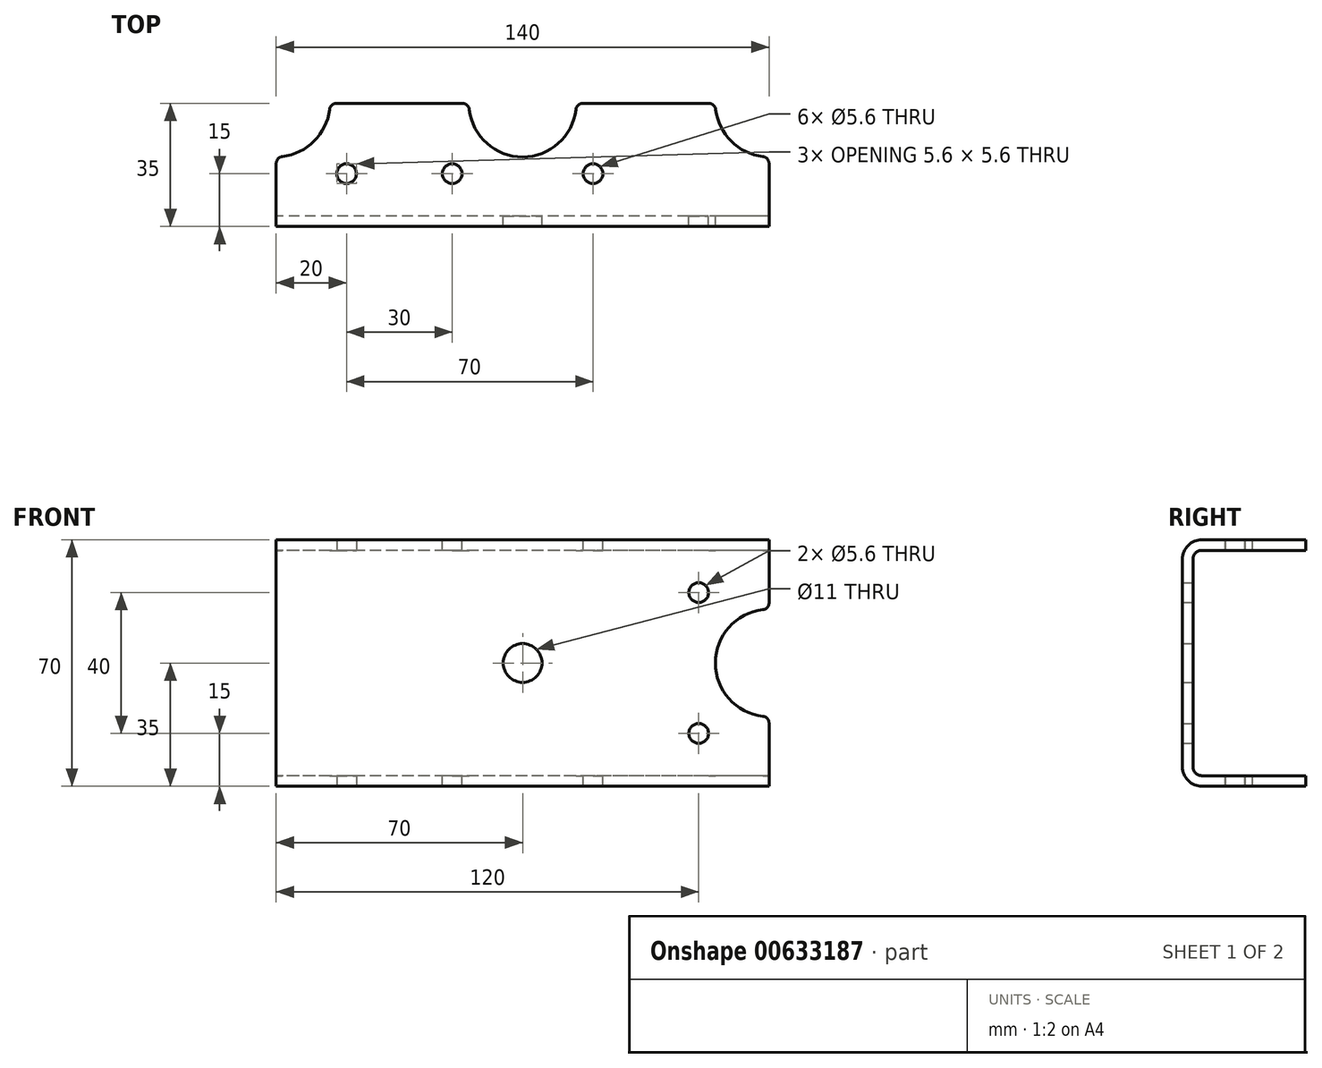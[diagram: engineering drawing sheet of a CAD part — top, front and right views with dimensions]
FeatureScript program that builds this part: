
annotation { "Feature Type Name" : "Feature", "Feature Type Description" : "" }
export const myFeature = defineFeature(function(context is Context, id is Id, definition is map)
    precondition{}
    {
        {
            var Q0;
            Q0=qCreatedBy(makeId("Front.planeOp"),FACE);
            var sketch = newSketch(context, id + "F0", { "sketchPlane" : qUnion([Q0])});
            skLineSegment(sketch, "E0.bottom", {"start": v(0, -32) * mm, "end": v(-32, -32) * mm});
            skLineSegment(sketch, "E0.top", {"start": v(0, 32) * mm, "end": v(-32, 32) * mm});
            skLineSegment(sketch, "E0.left", {"start": v(0, -32) * mm, "end": v(0, 32) * mm, "construction": true});
            skLineSegment(sketch, "E0.right", {"start": v(-32, -32) * mm, "end": v(-32, 32) * mm});
            skLineSegment(sketch, "E1.0", {"start": v(0, -35) * mm, "end": v(-35, -35) * mm});
            skLineSegment(sketch, "E1.1", {"start": v(-35, -35) * mm, "end": v(-35, 35) * mm});
            skLineSegment(sketch, "E1.2", {"start": v(0, 35) * mm, "end": v(-35, 35) * mm});
            skLineSegment(sketch, "E2", {"start": v(0, 35) * mm, "end": v(0, 32) * mm});
            skLineSegment(sketch, "E3", {"start": v(0, -32) * mm, "end": v(0, -35) * mm});
            skSolve(sketch);
        }
        {
            var Q0;
            Q0=makeQuery(id+"F0.imprint","IMPRINT",FACE,{"disambiguationData":[TD([[makeQuery(id+"F0.imprint","IMPRINT",EDGE,{"derivedFrom":sQuery(id+"F0.wireOp",EDGE,"E0.bottom")}),1.0]])]});
            extrude(context, id + "F1", {"entities" : qUnion([Q0]), "endBound" : BoundingType.SYMMETRIC, "depth" : 140 * mm});
        }
        {
            var Q0;
            Q0=makeQuery(id+"F1.opExtrude","SWEPT_EDGE",EDGE,{"disambiguationData":[OSD([sQuery(id+"F0.wireOp",EDGE,"E1.0"),sQuery(id+"F0.wireOp",EDGE,"E1.1")])]});
            var Q1;
            Q1=makeQuery(id+"F1.opExtrude","SWEPT_EDGE",EDGE,{"disambiguationData":[OSD([sQuery(id+"F0.wireOp",EDGE,"E1.1"),sQuery(id+"F0.wireOp",EDGE,"E1.2")])]});
            fillet(context, id + "F2", {"entities" : qUnion([Q0, Q1]), "radius" : 5.5 * mm, "tangentPropagation" : true, "allowEdgeOverflow" : false});
        }
        {
            var Q0;
            Q0=makeQuery(id+"F1.opExtrude","SWEPT_EDGE",EDGE,{"disambiguationData":[OSD([sQuery(id+"F0.wireOp",EDGE,"E0.top"),sQuery(id+"F0.wireOp",EDGE,"E0.right")])]});
            var Q1;
            Q1=makeQuery(id+"F1.opExtrude","SWEPT_EDGE",EDGE,{"disambiguationData":[OSD([sQuery(id+"F0.wireOp",EDGE,"E0.bottom"),sQuery(id+"F0.wireOp",EDGE,"E0.right")])]});
            fillet(context, id + "F3", {"entities" : qUnion([Q0, Q1]), "radius" : 2.5 * mm, "tangentPropagation" : true, "allowEdgeOverflow" : false});
        }
        {
            var Q0;
            Q0=qCreatedBy(makeId("Top.planeOp"),FACE);
            var sketch = newSketch(context, id + "F4", { "sketchPlane" : qUnion([Q0])});
            skCircle(sketch, "E4", {"center": v(0, -70) * mm, "radius": 15.25 * mm});
            skCircle(sketch, "E5", {"center": v(0, 70) * mm, "radius": 15.25 * mm});
            skSolve(sketch);
        }
        {
            var Q0;
            Q0=qSketchRegion(id+"F4",true);
            extrude(context, id + "F5", {"entities" : qUnion([Q0]), "operationType" : NewBodyOperationType.REMOVE, "endBound" : BoundingType.SYMMETRIC, "oppositeDirection" : true, "depth" : 70 * mm});
        }
        {
            var Q0;
            Q0=qCreatedBy(makeId("Top.planeOp"),FACE);
            var sketch = newSketch(context, id + "F6", { "sketchPlane" : qUnion([Q0])});
            skCircle(sketch, "E6", {"center": v(0, 0) * mm, "radius": 15.25 * mm});
            skSolve(sketch);
        }
        {
            var Q0;
            Q0=qSketchRegion(id+"F6",true);
            extrude(context, id + "F7", {"entities" : qUnion([Q0]), "operationType" : NewBodyOperationType.REMOVE, "endBound" : BoundingType.SYMMETRIC, "depth" : 70 * mm});
        }
        {
            var Q0;
            Q0=qCreatedBy(makeId("Top.planeOp"),FACE);
            var sketch = newSketch(context, id + "F8", { "sketchPlane" : qUnion([Q0])});
            skCircle(sketch, "E7", {"center": v(-20, 50) * mm, "radius": 2.8 * mm});
            skSolve(sketch);
        }
        {
            var Q0;
            Q0=qSketchRegion(id+"F8",true);
            extrude(context, id + "F9", {"entities" : qUnion([Q0]), "operationType" : NewBodyOperationType.REMOVE, "endBound" : BoundingType.SYMMETRIC, "depth" : 70 * mm});
        }
        {
            var Q0;
            Q0=qCreatedBy(makeId("Top.planeOp"),FACE);
            var sketch = newSketch(context, id + "F10", { "sketchPlane" : qUnion([Q0])});
            skCircle(sketch, "E8", {"center": v(-20, -20) * mm, "radius": 2.8 * mm});
            skCircle(sketch, "E9", {"center": v(-20, 20) * mm, "radius": 2.8 * mm});
            skSolve(sketch);
        }
        {
            var Q0;
            Q0=qSketchRegion(id+"F10",true);
            extrude(context, id + "F11", {"entities" : qUnion([Q0]), "operationType" : NewBodyOperationType.REMOVE, "endBound" : BoundingType.SYMMETRIC, "oppositeDirection" : true, "depth" : 70 * mm});
        }
        {
            var Q0;
            Q0=qCreatedBy(makeId("Right.planeOp"),FACE);
            var sketch = newSketch(context, id + "F12", { "sketchPlane" : qUnion([Q0])});
            skCircle(sketch, "E10", {"center": v(-70, 0) * mm, "radius": 15.25 * mm});
            skCircle(sketch, "E11", {"center": v(-50, 20) * mm, "radius": 2.8 * mm});
            skCircle(sketch, "E12", {"center": v(-50, -20) * mm, "radius": 2.8 * mm});
            skSolve(sketch);
        }
        {
            var Q0;
            Q0=qSketchRegion(id+"F12",true);
            extrude(context, id + "F13", {"entities" : qUnion([Q0]), "operationType" : NewBodyOperationType.REMOVE, "endBound" : BoundingType.THROUGH_ALL, "oppositeDirection" : true, "depth" : 25 * mm});
        }
        {
            var Q0;
            Q0=makeQuery(id+"F7.boolean.opBoolean","INTERSECT",EDGE,{"disambiguationData":[OD(0.0)],"derivedFrom":[makeQuery(id+"F1.opExtrude","SWEPT_FACE",FACE,{"disambiguationData":[OSD([sQuery(id+"F0.wireOp",EDGE,"E2")])]}),makeQuery(id+"F7.opExtrude","SWEPT_FACE",FACE,{"disambiguationData":[OSD([sQuery(id+"F6.wireOp",EDGE,"E6")])]})]});
            var Q1;
            Q1=makeQuery(id+"F7.boolean.opBoolean","INTERSECT",EDGE,{"disambiguationData":[OD(1.0)],"derivedFrom":[makeQuery(id+"F1.opExtrude","SWEPT_FACE",FACE,{"disambiguationData":[OSD([sQuery(id+"F0.wireOp",EDGE,"E2")])]}),makeQuery(id+"F7.opExtrude","SWEPT_FACE",FACE,{"disambiguationData":[OSD([sQuery(id+"F6.wireOp",EDGE,"E6")])]})]});
            var Q2;
            Q2=makeQuery(id+"F7.boolean.opBoolean","INTERSECT",EDGE,{"disambiguationData":[OD(1.0)],"derivedFrom":[makeQuery(id+"F1.opExtrude","SWEPT_FACE",FACE,{"disambiguationData":[OSD([sQuery(id+"F0.wireOp",EDGE,"E3")])]}),makeQuery(id+"F7.opExtrude","SWEPT_FACE",FACE,{"disambiguationData":[OSD([sQuery(id+"F6.wireOp",EDGE,"E6")])]})]});
            var Q3;
            Q3=makeQuery(id+"F7.boolean.opBoolean","INTERSECT",EDGE,{"disambiguationData":[OD(0.0)],"derivedFrom":[makeQuery(id+"F1.opExtrude","SWEPT_FACE",FACE,{"disambiguationData":[OSD([sQuery(id+"F0.wireOp",EDGE,"E3")])]}),makeQuery(id+"F7.opExtrude","SWEPT_FACE",FACE,{"disambiguationData":[OSD([sQuery(id+"F6.wireOp",EDGE,"E6")])]})]});
            fillet(context, id + "F14", {"entities" : qUnion([Q0, Q1, Q2, Q3]), "radius" : 2 * mm, "tangentPropagation" : true, "allowEdgeOverflow" : false});
        }
        {
            var Q0;
            Q0=makeQuery(id+"F5.boolean.opBoolean","INTERSECT",EDGE,{"disambiguationData":[OD(0.0)],"derivedFrom":[makeQuery(id+"F1.opExtrude","CAP_FACE",FACE,{"disambiguationData":[OSD([sQuery(id+"F0.wireOp",EDGE,"E0.bottom"),sQuery(id+"F0.wireOp",EDGE,"E0.top"),sQuery(id+"F0.wireOp",EDGE,"E0.right"),sQuery(id+"F0.wireOp",EDGE,"E1.0"),sQuery(id+"F0.wireOp",EDGE,"E1.1"),sQuery(id+"F0.wireOp",EDGE,"E1.2"),sQuery(id+"F0.wireOp",EDGE,"E2"),sQuery(id+"F0.wireOp",EDGE,"E3")])],"isStart":false}),makeQuery(id+"F5.opExtrude","SWEPT_FACE",FACE,{"disambiguationData":[OSD([sQuery(id+"F4.wireOp",EDGE,"E4")])]})]});
            var Q1;
            Q1=makeQuery(id+"F5.boolean.opBoolean","INTERSECT",EDGE,{"derivedFrom":[makeQuery(id+"F1.opExtrude","SWEPT_FACE",FACE,{"disambiguationData":[OSD([sQuery(id+"F0.wireOp",EDGE,"E2")])]}),makeQuery(id+"F5.opExtrude","SWEPT_FACE",FACE,{"disambiguationData":[OSD([sQuery(id+"F4.wireOp",EDGE,"E4")])]})]});
            var Q2;
            Q2=makeQuery(id+"F5.boolean.opBoolean","INTERSECT",EDGE,{"derivedFrom":[makeQuery(id+"F1.opExtrude","SWEPT_FACE",FACE,{"disambiguationData":[OSD([sQuery(id+"F0.wireOp",EDGE,"E3")])]}),makeQuery(id+"F5.opExtrude","SWEPT_FACE",FACE,{"disambiguationData":[OSD([sQuery(id+"F4.wireOp",EDGE,"E4")])]})]});
            var Q3;
            Q3=makeQuery(id+"F5.boolean.opBoolean","INTERSECT",EDGE,{"disambiguationData":[OD(1.0)],"derivedFrom":[makeQuery(id+"F1.opExtrude","CAP_FACE",FACE,{"disambiguationData":[OSD([sQuery(id+"F0.wireOp",EDGE,"E0.bottom"),sQuery(id+"F0.wireOp",EDGE,"E0.top"),sQuery(id+"F0.wireOp",EDGE,"E0.right"),sQuery(id+"F0.wireOp",EDGE,"E1.0"),sQuery(id+"F0.wireOp",EDGE,"E1.1"),sQuery(id+"F0.wireOp",EDGE,"E1.2"),sQuery(id+"F0.wireOp",EDGE,"E2"),sQuery(id+"F0.wireOp",EDGE,"E3")])],"isStart":false}),makeQuery(id+"F5.opExtrude","SWEPT_FACE",FACE,{"disambiguationData":[OSD([sQuery(id+"F4.wireOp",EDGE,"E4")])]})]});
            var Q4;
            Q4=makeQuery(id+"F13.boolean.opBoolean","INTERSECT",EDGE,{"disambiguationData":[OD(1.0)],"derivedFrom":[makeQuery(id+"F1.opExtrude","CAP_FACE",FACE,{"disambiguationData":[OSD([sQuery(id+"F0.wireOp",EDGE,"E0.bottom"),sQuery(id+"F0.wireOp",EDGE,"E0.top"),sQuery(id+"F0.wireOp",EDGE,"E0.right"),sQuery(id+"F0.wireOp",EDGE,"E1.0"),sQuery(id+"F0.wireOp",EDGE,"E1.1"),sQuery(id+"F0.wireOp",EDGE,"E1.2"),sQuery(id+"F0.wireOp",EDGE,"E2"),sQuery(id+"F0.wireOp",EDGE,"E3")])],"isStart":false}),makeQuery(id+"F13.opExtrude","SWEPT_FACE",FACE,{"disambiguationData":[OSD([sQuery(id+"F12.wireOp",EDGE,"E10")])]})]});
            var Q5;
            Q5=makeQuery(id+"F13.boolean.opBoolean","INTERSECT",EDGE,{"disambiguationData":[OD(0.0)],"derivedFrom":[makeQuery(id+"F1.opExtrude","CAP_FACE",FACE,{"disambiguationData":[OSD([sQuery(id+"F0.wireOp",EDGE,"E0.bottom"),sQuery(id+"F0.wireOp",EDGE,"E0.top"),sQuery(id+"F0.wireOp",EDGE,"E0.right"),sQuery(id+"F0.wireOp",EDGE,"E1.0"),sQuery(id+"F0.wireOp",EDGE,"E1.1"),sQuery(id+"F0.wireOp",EDGE,"E1.2"),sQuery(id+"F0.wireOp",EDGE,"E2"),sQuery(id+"F0.wireOp",EDGE,"E3")])],"isStart":false}),makeQuery(id+"F13.opExtrude","SWEPT_FACE",FACE,{"disambiguationData":[OSD([sQuery(id+"F12.wireOp",EDGE,"E10")])]})]});
            var Q6;
            Q6=makeQuery(id+"FLqxTyplpYU0jMX_1.1.F13.boolean.opBoolean","INTERSECT",EDGE,{"disambiguationData":[OD(0.0)],"derivedFrom":[makeQuery(id+"F1.opExtrude","CAP_FACE",FACE,{"disambiguationData":[OSD([sQuery(id+"F0.wireOp",EDGE,"E0.bottom"),sQuery(id+"F0.wireOp",EDGE,"E0.top"),sQuery(id+"F0.wireOp",EDGE,"E0.right"),sQuery(id+"F0.wireOp",EDGE,"E1.0"),sQuery(id+"F0.wireOp",EDGE,"E1.1"),sQuery(id+"F0.wireOp",EDGE,"E1.2"),sQuery(id+"F0.wireOp",EDGE,"E2"),sQuery(id+"F0.wireOp",EDGE,"E3")])],"isStart":true}),makeQuery(id+"FLqxTyplpYU0jMX_1.1.F13.opExtrude","SWEPT_FACE",FACE,{"disambiguationData":[OSD([sQuery(id+"F12.wireOp",EDGE,"E10")])]})]});
            var Q7;
            Q7=makeQuery(id+"F5.boolean.opBoolean","INTERSECT",EDGE,{"disambiguationData":[OD(1.0)],"derivedFrom":[makeQuery(id+"F1.opExtrude","CAP_FACE",FACE,{"disambiguationData":[OSD([sQuery(id+"F0.wireOp",EDGE,"E0.bottom"),sQuery(id+"F0.wireOp",EDGE,"E0.top"),sQuery(id+"F0.wireOp",EDGE,"E0.right"),sQuery(id+"F0.wireOp",EDGE,"E1.0"),sQuery(id+"F0.wireOp",EDGE,"E1.1"),sQuery(id+"F0.wireOp",EDGE,"E1.2"),sQuery(id+"F0.wireOp",EDGE,"E2"),sQuery(id+"F0.wireOp",EDGE,"E3")])],"isStart":true}),makeQuery(id+"F5.opExtrude","SWEPT_FACE",FACE,{"disambiguationData":[OSD([sQuery(id+"F4.wireOp",EDGE,"E5")])]})]});
            var Q8;
            Q8=makeQuery(id+"F5.boolean.opBoolean","INTERSECT",EDGE,{"derivedFrom":[makeQuery(id+"F1.opExtrude","SWEPT_FACE",FACE,{"disambiguationData":[OSD([sQuery(id+"F0.wireOp",EDGE,"E3")])]}),makeQuery(id+"F5.opExtrude","SWEPT_FACE",FACE,{"disambiguationData":[OSD([sQuery(id+"F4.wireOp",EDGE,"E5")])]})]});
            var Q9;
            Q9=makeQuery(id+"F5.boolean.opBoolean","INTERSECT",EDGE,{"disambiguationData":[OD(0.0)],"derivedFrom":[makeQuery(id+"F1.opExtrude","CAP_FACE",FACE,{"disambiguationData":[OSD([sQuery(id+"F0.wireOp",EDGE,"E0.bottom"),sQuery(id+"F0.wireOp",EDGE,"E0.top"),sQuery(id+"F0.wireOp",EDGE,"E0.right"),sQuery(id+"F0.wireOp",EDGE,"E1.0"),sQuery(id+"F0.wireOp",EDGE,"E1.1"),sQuery(id+"F0.wireOp",EDGE,"E1.2"),sQuery(id+"F0.wireOp",EDGE,"E2"),sQuery(id+"F0.wireOp",EDGE,"E3")])],"isStart":true}),makeQuery(id+"F5.opExtrude","SWEPT_FACE",FACE,{"disambiguationData":[OSD([sQuery(id+"F4.wireOp",EDGE,"E5")])]})]});
            var Q10;
            Q10=makeQuery(id+"F5.boolean.opBoolean","INTERSECT",EDGE,{"derivedFrom":[makeQuery(id+"F1.opExtrude","SWEPT_FACE",FACE,{"disambiguationData":[OSD([sQuery(id+"F0.wireOp",EDGE,"E2")])]}),makeQuery(id+"F5.opExtrude","SWEPT_FACE",FACE,{"disambiguationData":[OSD([sQuery(id+"F4.wireOp",EDGE,"E5")])]})]});
            var Q11;
            Q11=makeQuery(id+"FLqxTyplpYU0jMX_1.1.F13.boolean.opBoolean","INTERSECT",EDGE,{"disambiguationData":[OD(1.0)],"derivedFrom":[makeQuery(id+"F1.opExtrude","CAP_FACE",FACE,{"disambiguationData":[OSD([sQuery(id+"F0.wireOp",EDGE,"E0.bottom"),sQuery(id+"F0.wireOp",EDGE,"E0.top"),sQuery(id+"F0.wireOp",EDGE,"E0.right"),sQuery(id+"F0.wireOp",EDGE,"E1.0"),sQuery(id+"F0.wireOp",EDGE,"E1.1"),sQuery(id+"F0.wireOp",EDGE,"E1.2"),sQuery(id+"F0.wireOp",EDGE,"E2"),sQuery(id+"F0.wireOp",EDGE,"E3")])],"isStart":true}),makeQuery(id+"FLqxTyplpYU0jMX_1.1.F13.opExtrude","SWEPT_FACE",FACE,{"disambiguationData":[OSD([sQuery(id+"F12.wireOp",EDGE,"E10")])]})]});
            fillet(context, id + "F15", {"entities" : qUnion([Q0, Q1, Q2, Q3, Q4, Q5, Q6, Q7, Q8, Q9, Q10, Q11]), "radius" : 2 * mm, "tangentPropagation" : true, "allowEdgeOverflow" : false});
        }
        {
            var Q0;
            Q0=qCreatedBy(makeId("Right.planeOp"),FACE);
            var sketch = newSketch(context, id + "F16", { "sketchPlane" : qUnion([Q0])});
            skCircle(sketch, "E13", {"center": v(0, 0) * mm, "radius": 5.5 * mm});
            skSolve(sketch);
        }
        {
            var Q0;
            Q0=qSketchRegion(id+"F16",true);
            extrude(context, id + "F17", {"entities" : qUnion([Q0]), "operationType" : NewBodyOperationType.REMOVE, "endBound" : BoundingType.THROUGH_ALL, "oppositeDirection" : true, "depth" : 25 * mm});
        }
        {
            var Q0;
            Q0=makeQuery(id+"F1.opExtrude","SWEPT_BODY",BODY,{"disambiguationData":[OSD([sQuery(id+"F0.wireOp",EDGE,"E0.bottom"),sQuery(id+"F0.wireOp",EDGE,"E0.top"),sQuery(id+"F0.wireOp",EDGE,"E0.right"),sQuery(id+"F0.wireOp",EDGE,"E1.0"),sQuery(id+"F0.wireOp",EDGE,"E1.1"),sQuery(id+"F0.wireOp",EDGE,"E1.2"),sQuery(id+"F0.wireOp",EDGE,"E2"),sQuery(id+"F0.wireOp",EDGE,"E3")])]});
            var Q1;
            {var subQ0=sQuery(id+"F0.wireOp",EDGE,"E0.right");var subQ1=sQuery(id+"F0.wireOp",EDGE,"E0.top");Q1=makeQuery(id+"F13.boolean.opBoolean","SPLIT",EDGE,{"disambiguationData":[TD([makeQuery(id+"F3.opFillet","BLEND_FACE",FACE,{"disambiguationData":[OSD([subQ1,subQ0])]})])],"derivedFrom":makeQuery(id+"F1.opExtrude","CAP_EDGE",EDGE,{"disambiguationData":[OSD([subQ0])],"isStart":false})});}
            transform(context, id + "F18", {"entities" : qUnion([Q0]), "transformType" : TransformType.ROTATION, "transformAxis" : qUnion([Q1]), "angle" : 90 * degree, "makeCopy" : false});
        }
        {
            var Q0;
            Q0=makeQuery(id+"F1.opExtrude","SWEPT_BODY",BODY,{"disambiguationData":[OSD([sQuery(id+"F0.wireOp",EDGE,"E0.bottom"),sQuery(id+"F0.wireOp",EDGE,"E0.top"),sQuery(id+"F0.wireOp",EDGE,"E0.right"),sQuery(id+"F0.wireOp",EDGE,"E1.0"),sQuery(id+"F0.wireOp",EDGE,"E1.1"),sQuery(id+"F0.wireOp",EDGE,"E1.2"),sQuery(id+"F0.wireOp",EDGE,"E2"),sQuery(id+"F0.wireOp",EDGE,"E3")])]});
            transform(context, id + "F19", {"entities" : qUnion([Q0]), "transformType" : TransformType.TRANSLATION_3D, "dx" : 32 * mm, "dy" : 38 * mm, "dz" : 35 * mm, "makeCopy" : false});
        }
    });
